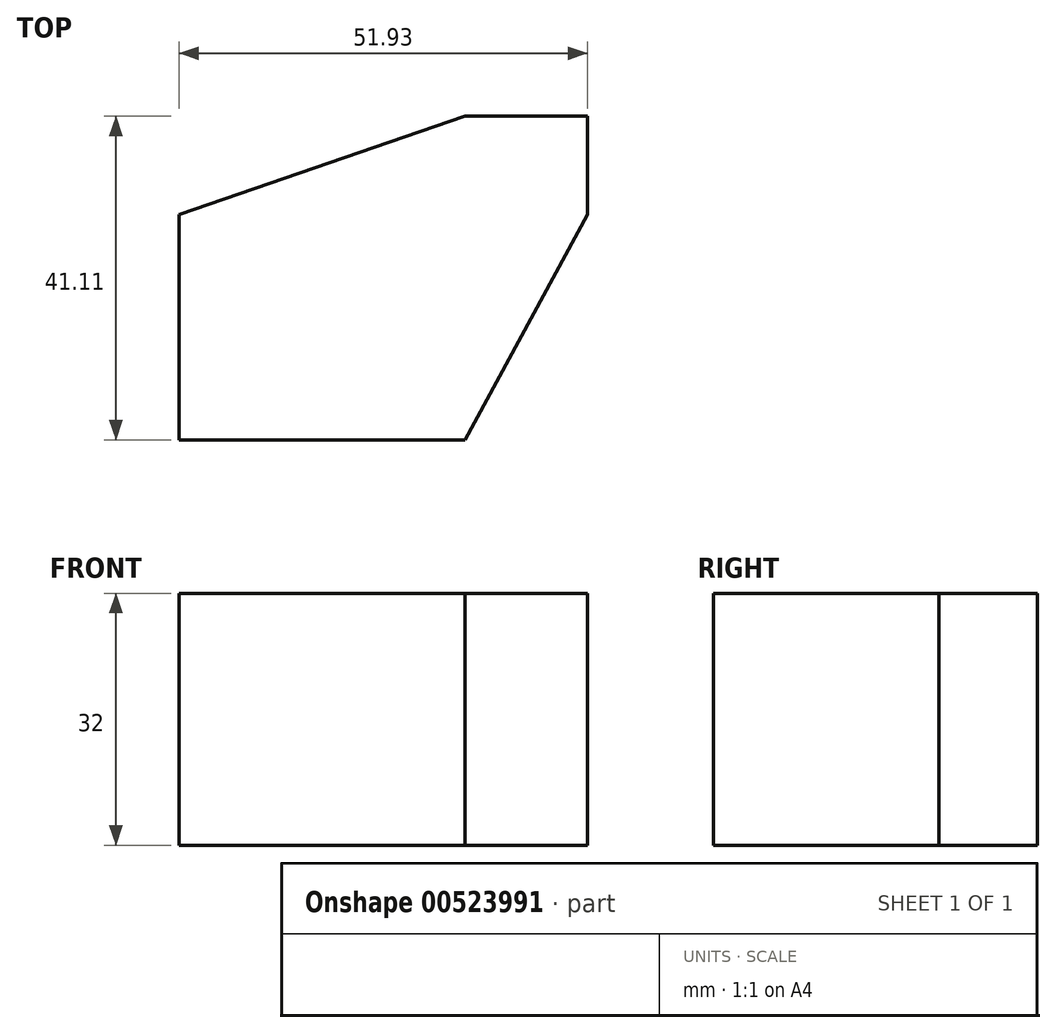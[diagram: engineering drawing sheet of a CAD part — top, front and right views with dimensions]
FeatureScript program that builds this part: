
annotation { "Feature Type Name" : "Feature", "Feature Type Description" : "" }
export const myFeature = defineFeature(function(context is Context, id is Id, definition is map)
    precondition{}
    {
        {
            var Q0;
            Q0=qCreatedBy(makeId("Top.planeOp"),FACE);
            var sketch = newSketch(context, id + "F0", { "sketchPlane" : qUnion([Q0])});
            skLineSegment(sketch, "E0.bottom", {"start": v(20.34, -7.9) * mm, "end": v(-16, -7.9) * mm});
            skLineSegment(sketch, "E0.top", {"start": v(20.34, 20.73) * mm, "end": v(-16, 20.73) * mm});
            skLineSegment(sketch, "E0.left", {"start": v(20.34, -7.9) * mm, "end": v(20.34, 20.73) * mm});
            skLineSegment(sketch, "E0.right", {"start": v(-16, -7.9) * mm, "end": v(-16, 20.73) * mm});
            skLineSegment(sketch, "E1.bottom", {"start": v(20.34, 20.73) * mm, "end": v(10.88, 20.73) * mm});
            skLineSegment(sketch, "E1.top", {"start": v(20.34, 20.73) * mm, "end": v(10.88, 20.73) * mm});
            skLineSegment(sketch, "E1.left", {"start": v(20.34, 20.73) * mm, "end": v(20.34, 20.73) * mm});
            skLineSegment(sketch, "E1.right", {"start": v(10.88, 20.73) * mm, "end": v(10.88, 20.73) * mm});
            skLineSegment(sketch, "E2.bottom", {"start": v(20.34, 20.73) * mm, "end": v(35.93, 20.73) * mm});
            skLineSegment(sketch, "E2.top", {"start": v(20.34, 33.21) * mm, "end": v(35.93, 33.21) * mm});
            skLineSegment(sketch, "E2.left", {"start": v(20.34, 20.73) * mm, "end": v(20.34, 33.21) * mm});
            skLineSegment(sketch, "E2.right", {"start": v(35.93, 20.73) * mm, "end": v(35.93, 33.21) * mm});
            skLineSegment(sketch, "E3", {"start": v(-16, 20.73) * mm, "end": v(20.34, 33.21) * mm});
            skLineSegment(sketch, "E4", {"start": v(35.93, 20.73) * mm, "end": v(20.34, -7.9) * mm});
            skSolve(sketch);
        }
        {
            var Q0;
            Q0 = qSketchRegion(id + "F0", true);
            extrude(context, id + "F1", {"entities" : qUnion([Q0]), "depth" : 32 * mm, "offsetDistance" : 25.4 * mm});
        }
    });
